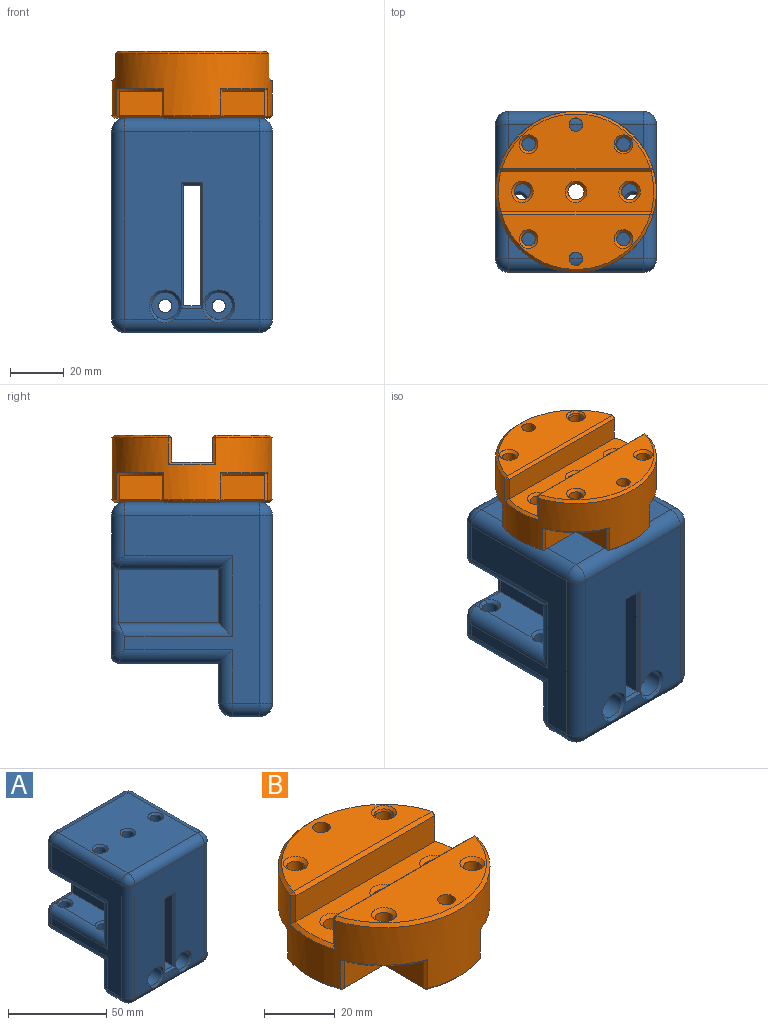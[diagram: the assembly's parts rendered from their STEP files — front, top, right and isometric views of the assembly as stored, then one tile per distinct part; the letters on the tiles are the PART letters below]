
ASSEMBLY  parts=2 mates=1
PART A: 144 faces, bbox 60x60x80 mm
  f0: plane 13.37x5mm, normal (0,-1,0), area 40mm2, adj f1,f139,f140,f141,f142,f143
  f1: cone r=5mm half-angle=45deg, axis (0,-1,0), area 39.8mm2, adj f0,f2,f137,f138
  f2: plane 70x50mm, normal (0,-1,0), area 2866.9mm2, adj f1,f3,f134,f135,f136,f139,f141,f142
  f3: plane 8x1mm, normal (0,-0.71,-0.71), area 9.9mm2, adj f2,f4,f139,f141
  f4: plane 56.5x15mm, normal (0,0,-1), area 627.2mm2, adj f3,f5,f8,f119,f120,f121,f130,f131
  f5: plane 46x1mm, normal (-0.71,0.71,0), area 64.3mm2, adj f4,f6,f121,f132
  f6: plane 8x1mm, normal (0,0.71,0.71), area 9.9mm2, adj f5,f7,f121,f130
  f7: plane 18x6mm, normal (0,0,1), area 108mm2, adj f6,f131,f132,f140
  f8: plane 37.5x30mm, normal (-1,0,0), area 1125mm2, adj f4,f9,f118,f121
  f9: cylinder r=5mm len=37.5mm, axis (0,-1,0), area 294.5mm2, adj f8,f10,f117,f121
  f10: plane 37.5x12.5mm, normal (0,0,-1), area 312.4mm2, adj f9,f11,f110,f111,f112,f113,f114,f115
  f11: cone r=3mm half-angle=45deg, axis (0,0,-1), area 19.1mm2, adj f10,f12,f15,f16
  f12: bspline ~3.87x1.5mm, area 5.3mm2, adj f11,f13,f16,f116
  f13: cone r=3mm half-angle=45deg, axis (0,0,-1), area 3.5mm2, adj f12,f14,f15,f16
  f14: plane 2.11x1.81mm, normal (0,0,-1), area 1.4mm2, adj f13,f110,f116
  f15: bspline ~2.78x1.35mm, area 3.8mm2, adj f11,f13,f16,f110
  f16: cylinder r=3mm len=13mm, axis (0,0,-1), area 245mm2, adj f11,f12,f13,f15,f17,f107,f108,f109
  f17: cone r=3mm half-angle=45deg, axis (0,0,1), area 19.1mm2, adj f16,f18,f107,f109
  f18: plane 37.5x12.5mm, normal (0,0,1), area 312.4mm2, adj f17,f19,f23,f97,f98,f99,f106,f113
  f19: cone r=4mm half-angle=45deg, axis (0,0,1), area 26.1mm2, adj f18,f20,f22
  f20: cylinder r=3mm len=13mm, axis (0,0,-1), area 245mm2, adj f19,f21,f22,f111
  f21: bspline ~3.87x1.5mm, area 5.3mm2, adj f20,f111,f112
  f22: bspline ~3.87x1.5mm, area 5.3mm2, adj f19,f20,f23
  f23: cylinder r=5mm len=19.25mm, axis (0,1,0), area 129.9mm2, adj f18,f22,f24,f96,f113
  f24: plane 70x50mm, normal (1,0,0), area 1396.3mm2, adj f23,f25,f90,f92,f94,f95,f96,f112
  f25: cylinder r=5mm len=20mm, axis (0,0,-1), area 137.4mm2, adj f24,f26,f112,f121
  f26: sphere r=5mm, area 39.3mm2, adj f25,f27,f90
  f27: cylinder r=5mm len=50mm, axis (-1,0,0), area 392.7mm2, adj f26,f28,f89,f121
  f28: sphere r=5mm, area 53.5mm2, adj f27,f29,f87
  f29: cylinder r=5mm len=20mm, axis (0,0,1), area 137.4mm2, adj f28,f30,f86,f121
  f30: cylinder r=5mm len=42.5mm, axis (0,-1,0), area 295.7mm2, adj f29,f31,f82,f83,f84,f85,f86
  f31: bspline ~5.97x5mm, area 13.6mm2, adj f30,f32,f81
  f32: cylinder r=5mm len=10mm, axis (0,0,-1), area 58.9mm2, adj f31,f33,f80,f86
  f33: bspline ~5.25x5mm, area 13.6mm2, adj f32,f34,f79
  f34: cylinder r=2.5mm len=15mm, axis (-1,0,0), area 53.2mm2, adj f33,f35,f65,f77,f78,f80
  f35: cylinder r=2.5mm len=32.5mm, axis (0,0,-1), area 211.1mm2, adj f34,f36,f38,f64,f80,f119,f120
  f36: torus R=2.5mm, axis (0,-1,0), area 25.2mm2, adj f35,f37,f80,f81
  f37: cylinder r=5mm len=37.5mm, axis (0,1,0), area 294.5mm2, adj f36,f83,f120,f121
  f38: cylinder r=2.5mm len=15mm, axis (1,0,0), area 54mm2, adj f35,f39,f62,f63
  f39: plane 37.5x12.5mm, normal (0,0,-1), area 418.5mm2, adj f38,f40,f42,f61,f64
  f40: plane 20x12.5mm, normal (0,1,0), area 250mm2, adj f39,f41,f64,f65
  f41: cylinder r=5mm len=30mm, axis (0,0,1), area 196.3mm2, adj f40,f42,f79,f86
  f42: cylinder r=5mm len=42.5mm, axis (0,-1,0), area 304.3mm2, adj f39,f41,f43,f63,f86
  f43: bspline ~3.65x3.65mm, area 1.9mm2, adj f42,f44
  f44: cylinder r=5mm len=17.5mm, axis (0,0,-1), area 127.6mm2, adj f43,f45,f62,f63,f86
  f45: sphere r=5mm, area 53.5mm2, adj f44,f46,f59
  f46: cylinder r=5mm len=50mm, axis (0,1,0), area 392.7mm2, adj f45,f47,f58,f86
  f47: plane 50x50mm, normal (0,0,1), area 2349.2mm2, adj f46,f48,f54,f56,f59,f92,f135
  f48: cone r=3mm half-angle=45deg, axis (0,0,1), area 31.1mm2, adj f47,f49
  f49: cylinder r=3mm len=23mm, axis (0,0,-1), area 433.5mm2, adj f48,f50
  f50: cone r=4mm half-angle=45deg, axis (0,0,-1), area 31.1mm2, adj f49,f51
  f51: plane 37.5x12.5mm, normal (0,0,-1), area 418.5mm2, adj f50,f52,f95,f97,f98
  f52: cylinder r=2.5mm len=15mm, axis (1,0,0), area 54mm2, adj f51,f53,f62,f118
  f53: bspline ~5.25x5mm, area 13.6mm2, adj f52,f94,f95
  f54: cone r=3mm half-angle=45deg, axis (0,0,1), area 31.1mm2, adj f47,f55
  f55: cylinder r=3mm len=23mm, axis (0,0,-1), area 433.5mm2, adj f54,f133
  f56: cone r=4mm half-angle=45deg, axis (0,0,1), area 31.1mm2, adj f47,f57
  f57: cylinder r=3mm len=23mm, axis (0,0,-1), area 433.5mm2, adj f56,f61
  f58: sphere r=5mm, area 39.3mm2, adj f46,f134,f135
  f59: cylinder r=5mm len=50mm, axis (-1,0,0), area 392.7mm2, adj f45,f47,f60,f62
  f60: sphere r=5mm, area 25mm2, adj f59,f92,f94
  f61: cone r=3mm half-angle=45deg, axis (0,0,-1), area 31.1mm2, adj f39,f57
  f62: plane 50x17.5mm, normal (0,1,0), area 875mm2, adj f38,f44,f52,f59,f94,f119
  f63: bspline ~4.67x3.48mm, area 8.4mm2, adj f38,f42,f44
  f64: plane 37.5x20mm, normal (-1,0,0), area 750mm2, adj f35,f39,f40,f65
  f65: plane 37.5x12.5mm, normal (0,0,1), area 369.9mm2, adj f34,f40,f64,f66,f73,f79
  f66: cone r=3mm half-angle=45deg, axis (0,0,1), area 19.1mm2, adj f65,f67,f69,f77
  f67: bspline ~3.87x1.5mm, area 5.3mm2, adj f66,f68,f69,f79
  f68: cone r=3mm half-angle=45deg, axis (0,0,1), area 3.5mm2, adj f67,f69,f77,f78
  f69: cylinder r=3mm len=13mm, axis (0,0,-1), area 245mm2, adj f66,f67,f68,f70,f71,f72,f77,f84
  f70: bspline ~2.78x1.35mm, area 3.8mm2, adj f69,f71,f72,f81
  f71: cone r=4mm half-angle=45deg, axis (0,0,-1), area 19.1mm2, adj f69,f70,f83,f84
  f72: cone r=4mm half-angle=45deg, axis (0,0,-1), area 3.5mm2, adj f69,f70,f84,f85
  f73: cone r=4mm half-angle=45deg, axis (0,0,1), area 26.1mm2, adj f65,f74,f76
  f74: cylinder r=3mm len=13mm, axis (0,0,-1), area 245mm2, adj f73,f75,f76,f82
  f75: cone r=3mm half-angle=45deg, axis (0,0,-1), area 26.1mm2, adj f74,f82,f83
  f76: bspline ~3.87x1.5mm, area 5.3mm2, adj f73,f74,f79
  f77: bspline ~2.78x1.35mm, area 3.8mm2, adj f34,f66,f68,f69
  f78: plane 2.11x1.81mm, normal (0,0,1), area 1.4mm2, adj f34,f68,f79
  f79: cylinder r=5mm len=42.5mm, axis (0,1,0), area 295.7mm2, adj f33,f41,f65,f67,f76,f78,f86
  f80: plane 15x10mm, normal (0,1,0), area 148.7mm2, adj f32,f34,f35,f36,f81
  f81: cylinder r=2.5mm len=12.5mm, axis (1,0,0), area 48.3mm2, adj f31,f36,f70,f80,f83,f85
  f82: bspline ~3.87x1.5mm, area 5.3mm2, adj f30,f74,f75
  f83: plane 37.5x12.5mm, normal (0,0,-1), area 369.9mm2, adj f30,f37,f71,f75,f81,f121
  f84: bspline ~3.87x1.5mm, area 5.3mm2, adj f30,f69,f71,f72
  f85: plane 2.11x1.81mm, normal (0,0,-1), area 1.4mm2, adj f30,f72,f81
  f86: plane 70x50mm, normal (-1,0,0), area 1500mm2, adj f29,f30,f32,f41,f42,f44,f46,f79
  f87: cylinder r=5mm len=10mm, axis (0,-1,0), area 78.5mm2, adj f28,f86,f88,f89
  f88: sphere r=5mm, area 39.3mm2, adj f87,f134,f143
  f89: plane 50x10mm, normal (0,0,-1), area 500mm2, adj f27,f87,f90,f143
  f90: cylinder r=5mm len=10mm, axis (0,1,0), area 78.5mm2, adj f24,f26,f89,f91
  f91: sphere r=5mm, area 39.3mm2, adj f90,f136,f143
  f92: cylinder r=5mm len=50mm, axis (0,-1,0), area 392.7mm2, adj f24,f47,f60,f93
  f93: sphere r=5mm, area 39.3mm2, adj f92,f135,f136
  f94: cylinder r=5mm len=17.5mm, axis (0,0,1), area 127.6mm2, adj f24,f53,f60,f62
  f95: cylinder r=5mm len=42.5mm, axis (0,-1,0), area 304.3mm2, adj f24,f51,f53,f96
  f96: cylinder r=5mm len=30mm, axis (0,0,-1), area 196.3mm2, adj f23,f24,f95,f97
  f97: plane 20x12.5mm, normal (0,1,0), area 250mm2, adj f18,f51,f96,f98
  f98: plane 37.5x20mm, normal (1,0,0), area 750mm2, adj f18,f51,f97,f118
  f99: cylinder r=2.5mm len=15mm, axis (-1,0,0), area 53.2mm2, adj f18,f100,f104,f105,f109,f118
  f100: plane 15x10mm, normal (0,1,0), area 148.7mm2, adj f99,f101,f110,f117,f118
  f101: cylinder r=5mm len=10mm, axis (0,0,1), area 58.9mm2, adj f100,f102,f103,f104
  f102: bspline ~5.97x5mm, area 13.6mm2, adj f101,f110,f116
  f103: plane 9.25x5mm, normal (1,0,0), area 46.2mm2, adj f101,f106,f115,f116
  f104: bspline ~5.97x5mm, area 13.6mm2, adj f99,f101,f106
  f105: plane 2.11x1.81mm, normal (0,0,1), area 1.4mm2, adj f99,f106,f108
  f106: cylinder r=5mm len=11.75mm, axis (0,1,0), area 80.8mm2, adj f18,f103,f104,f105,f107,f115
  f107: bspline ~3.87x1.5mm, area 5.3mm2, adj f16,f17,f106,f108
  f108: cone r=3mm half-angle=45deg, axis (0,0,1), area 3.5mm2, adj f16,f105,f107,f109
  f109: bspline ~2.78x1.35mm, area 3.8mm2, adj f16,f17,f99,f108
  f110: cylinder r=2.5mm len=12.5mm, axis (1,0,0), area 48.3mm2, adj f10,f14,f15,f100,f102,f117
  f111: cone r=4mm half-angle=45deg, axis (0,0,-1), area 26.1mm2, adj f10,f20,f21
  f112: cylinder r=5mm len=19.25mm, axis (0,1,0), area 129.9mm2, adj f10,f21,f24,f25,f113
  f113: plane 15x10mm, normal (0,1,0), area 139.3mm2, adj f10,f18,f23,f24,f112,f114
  f114: plane 15x11.5mm, normal (1,0,0), area 172.5mm2, adj f10,f18,f113,f115
  f115: plane 15x10mm, normal (0,-1,0), area 139.3mm2, adj f10,f18,f103,f106,f114,f116
  f116: cylinder r=5mm len=11.75mm, axis (0,1,0), area 80.8mm2, adj f10,f12,f14,f102,f103,f115
  f117: torus R=2.5mm, axis (0,-1,0), area 25.2mm2, adj f9,f100,f110,f118
  f118: cylinder r=2.5mm len=32.5mm, axis (0,0,1), area 211.1mm2, adj f8,f52,f98,f99,f100,f117,f119
  f119: cylinder r=2.5mm len=20mm, axis (1,0,0), area 68.7mm2, adj f4,f35,f62,f118
  f120: plane 37.5x30mm, normal (1,0,0), area 1125mm2, adj f4,f35,f37,f121
  f121: plane 50x50mm, normal (0,1,0), area 840.8mm2, adj f4,f5,f6,f8,f9,f10,f25,f27
  f122: cone r=2.5mm half-angle=45deg, axis (0,1,0), area 26.7mm2, adj f121,f123
  f123: cylinder r=2.5mm len=11.5mm, axis (0,1,0), area 180.6mm2, adj f122,f124
  f124: plane 10x10mm, normal (0,-1,0), area 58.9mm2, adj f123,f125
  f125: cylinder r=5mm len=10mm, axis (0,-1,0), area 203.8mm2, adj f124,f126,f142
  f126: bspline ~6.63x2.08mm, area 10mm2, adj f125,f142,f143
  f127: cone r=3.5mm half-angle=45deg, axis (0,1,0), area 26.7mm2, adj f121,f128
  f128: cylinder r=2.5mm len=11.5mm, axis (0,1,0), area 180.6mm2, adj f127,f129
  f129: plane 10x10mm, normal (0,-1,0), area 58.9mm2, adj f128,f137
  f130: plane 46x1mm, normal (0.71,0.71,0), area 64.3mm2, adj f4,f6,f121,f131
  f131: plane 45x18mm, normal (1,0,0), area 810mm2, adj f4,f7,f130,f139
  f132: plane 45x18mm, normal (-1,0,0), area 810mm2, adj f4,f5,f7,f141
  f133: cone r=4mm half-angle=45deg, axis (0,0,-1), area 31.1mm2, adj f4,f55
  f134: cylinder r=5mm len=70mm, axis (0,0,1), area 549.8mm2, adj f2,f58,f86,f88
  f135: cylinder r=5mm len=50mm, axis (1,0,0), area 392.7mm2, adj f2,f47,f58,f93
  f136: cylinder r=5mm len=70mm, axis (0,0,-1), area 549.8mm2, adj f2,f24,f91,f93
  f137: cylinder r=5mm len=10mm, axis (0,-1,0), area 203.8mm2, adj f1,f129,f138
  f138: bspline ~6.63x2.08mm, area 10mm2, adj f1,f137,f143
  f139: plane 47x1mm, normal (0.71,-0.71,0), area 65.1mm2, adj f0,f2,f3,f131,f140
  f140: plane 8x1mm, normal (0,-0.71,0.71), area 9.9mm2, adj f0,f7,f139,f141
  f141: plane 47x1mm, normal (-0.71,-0.71,0), area 65.1mm2, adj f0,f2,f3,f132,f140
  f142: cone r=5mm half-angle=45deg, axis (0,-1,0), area 39.8mm2, adj f0,f2,f125,f126
  f143: cylinder r=5mm len=50mm, axis (-1,0,0), area 381.4mm2, adj f0,f2,f88,f89,f91,f126,f138
PART B: 83 faces, bbox 60x60x25 mm
  f0: plane 58x58mm, normal (0,0,-1), area 1669.7mm2, adj f35,f36,f37,f52,f53,f54,f55,f58
  f1: plane 58x15.57mm, normal (0,0,1), area 709.6mm2, adj f23,f24,f30,f31,f32,f42,f43,f44
  f2: plane 55.45x20.5mm, normal (0,0,1), area 738.6mm2, adj f10,f33,f34,f38,f39
  f3: cylinder r=30mm len=60mm, axis (0,0,-1), area 2954.1mm2, adj f39,f42,f43,f44,f45,f46,f47,f48
  f4: cylinder r=2.5mm len=13mm, axis (0,0,1), area 204.2mm2, adj f28,f60
  f5: cylinder r=2.5mm len=12.59mm, axis (0,0,1), area 197.7mm2, adj f56,f57
  f6: cylinder r=2.5mm len=13mm, axis (0,0,1), area 204.2mm2, adj f33,f61
  f7: cylinder r=2.5mm len=13mm, axis (0,0,1), area 204.2mm2, adj f34,f62
  f8: plane 55.45x20.5mm, normal (0,0,1), area 738.6mm2, adj f9,f28,f29,f48,f51
  f9: cylinder r=2.5mm len=24mm, axis (0,0,-1), area 377mm2, adj f8,f58
  f10: cylinder r=2.5mm len=24mm, axis (0,0,-1), area 377mm2, adj f2,f59
  f11: plane 15.98x9.37mm, normal (0,-1,0), area 143.9mm2, adj f12,f13,f79,f81,f82
  f12: plane 15.98x9.37mm, normal (-1,0,0), area 143.9mm2, adj f11,f13,f78,f79,f80
  f13: plane 15.58x15.58mm, normal (0,0,-1), area 115.1mm2, adj f11,f12,f62,f79
  f14: plane 15.98x9.37mm, normal (1,0,0), area 143.9mm2, adj f15,f16,f65,f66,f67
  f15: plane 15.98x9.37mm, normal (0,-1,0), area 143.9mm2, adj f14,f16,f63,f64,f65
  f16: plane 15.58x15.58mm, normal (0,0,-1), area 115.1mm2, adj f14,f15,f61,f65
  f17: plane 15.98x9.37mm, normal (0,1,0), area 143.9mm2, adj f18,f19,f68,f69,f70
  f18: plane 15.98x9.37mm, normal (1,0,0), area 143.9mm2, adj f17,f19,f69,f71,f72
  f19: plane 15.58x15.58mm, normal (0,0,-1), area 115.1mm2, adj f17,f18,f57,f69
  f20: plane 15.98x9.37mm, normal (-1,0,0), area 143.9mm2, adj f21,f22,f74,f76,f77
  f21: plane 15.98x9.37mm, normal (0,1,0), area 143.9mm2, adj f20,f22,f73,f75,f77
  f22: plane 15.58x15.58mm, normal (0,0,-1), area 115.1mm2, adj f20,f21,f60,f77
  f23: plane 55.45x9mm, normal (0,-1,0), area 499.1mm2, adj f1,f46,f47,f51
  f24: plane 55.45x9mm, normal (0,1,0), area 499.1mm2, adj f1,f38,f42,f43
  f25: cylinder r=3mm len=13mm, axis (0,0,1), area 245mm2, adj f30,f37
  f26: cylinder r=3mm len=13mm, axis (0,0,1), area 245mm2, adj f31,f36
  f27: cylinder r=3mm len=13mm, axis (0,0,1), area 245mm2, adj f32,f35
  f28: cone r=2.5mm half-angle=45deg, axis (0,0,1), area 26.7mm2, adj f4,f8
  f29: cone r=3.5mm half-angle=45deg, axis (0,0,1), area 19.8mm2, adj f8,f56
  f30: cone r=3mm half-angle=45deg, axis (0,0,1), area 31.1mm2, adj f1,f25
  f31: cone r=3mm half-angle=45deg, axis (0,0,1), area 31.1mm2, adj f1,f26
  f32: cone r=4mm half-angle=45deg, axis (0,0,1), area 31.1mm2, adj f1,f27
  f33: cone r=2.5mm half-angle=45deg, axis (0,0,1), area 26.7mm2, adj f2,f6
  f34: cone r=3.5mm half-angle=45deg, axis (0,0,1), area 26.7mm2, adj f2,f7
  f35: cone r=3mm half-angle=45deg, axis (0,0,-1), area 31.1mm2, adj f0,f27
  f36: cone r=4mm half-angle=45deg, axis (0,0,-1), area 31.1mm2, adj f0,f26
  f37: cone r=4mm half-angle=45deg, axis (0,0,-1), area 31.1mm2, adj f0,f25
  f38: plane 55.45x1mm, normal (0,0.71,0.71), area 78.4mm2, adj f2,f24,f40,f41
  f39: cone r=29mm half-angle=45deg, axis (0,0,-1), area 106.2mm2, adj f2,f3,f40,f41
  f40: plane 1.29x1mm, normal (0.69,0.51,0.51), area 0.9mm2, adj f38,f39,f42
  f41: plane 1.29x1mm, normal (-0.69,0.51,0.51), area 0.9mm2, adj f38,f39,f43
  f42: plane 10.01x1.31mm, normal (0.8,0.59,0), area 15.1mm2, adj f1,f3,f24,f40,f44
  f43: plane 10.01x1.31mm, normal (-0.8,0.59,0), area 15.1mm2, adj f1,f3,f24,f41,f45
  f44: cone r=29mm half-angle=45deg, axis (0,0,-1), area 23.8mm2, adj f1,f3,f42,f46
  f45: cone r=29mm half-angle=45deg, axis (0,0,-1), area 23.8mm2, adj f1,f3,f43,f47
  f46: plane 10.01x1.31mm, normal (0.8,-0.59,0), area 15.1mm2, adj f1,f3,f23,f44,f49
  f47: plane 10.01x1.31mm, normal (-0.8,-0.59,0), area 15.1mm2, adj f1,f3,f23,f45,f50
  f48: cone r=29mm half-angle=45deg, axis (0,0,-1), area 106.2mm2, adj f3,f8,f49,f50
  f49: plane 1.29x1mm, normal (0.69,-0.51,0.51), area 0.9mm2, adj f46,f48,f51
  f50: plane 1.29x1mm, normal (-0.69,-0.51,0.51), area 0.9mm2, adj f47,f48,f51
  f51: plane 55.45x1mm, normal (0,-0.71,0.71), area 78.4mm2, adj f8,f23,f49,f50
  f52: cone r=30mm half-angle=45deg, axis (0,0,1), area 30.6mm2, adj f0,f3,f71,f72,f74,f76
  f53: cone r=30mm half-angle=45deg, axis (0,0,1), area 30.6mm2, adj f0,f3,f63,f64,f68,f70
  f54: cone r=30mm half-angle=45deg, axis (0,0,1), area 30.6mm2, adj f0,f3,f66,f67,f78,f80
  f55: cone r=30mm half-angle=45deg, axis (0,0,1), area 30.6mm2, adj f0,f3,f73,f75,f81,f82
  f56: cone r=2.5mm half-angle=22.5deg, axis (0,0,1), area 12.7mm2, adj f5,f29
  f57: cone r=3.5mm half-angle=45deg, axis (0,0,-1), area 26.7mm2, adj f5,f19
  f58: cone r=3.5mm half-angle=45deg, axis (0,0,-1), area 26.7mm2, adj f0,f9
  f59: cone r=2.5mm half-angle=45deg, axis (0,0,-1), area 26.7mm2, adj f0,f10
  f60: cone r=3.5mm half-angle=45deg, axis (0,0,-1), area 26.7mm2, adj f4,f22
  f61: cone r=2.5mm half-angle=45deg, axis (0,0,-1), area 26.7mm2, adj f6,f16
  f62: cone r=3.5mm half-angle=45deg, axis (0,0,-1), area 26.7mm2, adj f7,f13
  f63: plane 10.34x0.95mm, normal (0.57,-0.82,0), area 11.2mm2, adj f3,f15,f53,f64,f65
  f64: plane 17.45x1mm, normal (0,-0.71,-0.71), area 23.6mm2, adj f0,f15,f53,f63,f66
  f65: cone r=29mm half-angle=45deg, axis (0,0,1), area 33.7mm2, adj f3,f14,f15,f16,f63,f67
  f66: plane 17.45x1mm, normal (0.71,0,-0.71), area 23.6mm2, adj f0,f14,f54,f64,f67
  f67: plane 10.34x0.95mm, normal (0.82,-0.57,0), area 11.2mm2, adj f3,f14,f54,f65,f66
  f68: plane 10.34x0.95mm, normal (0.57,0.82,0), area 11.2mm2, adj f3,f17,f53,f69,f70
  f69: cone r=29mm half-angle=45deg, axis (0,0,1), area 33.7mm2, adj f3,f17,f18,f19,f68,f71
  f70: plane 17.45x1mm, normal (0,0.71,-0.71), area 23.6mm2, adj f0,f17,f53,f68,f72
  f71: plane 10.34x0.95mm, normal (0.82,0.57,0), area 11.2mm2, adj f3,f18,f52,f69,f72
  f72: plane 17.45x1mm, normal (0.71,0,-0.71), area 23.6mm2, adj f0,f18,f52,f70,f71
  f73: plane 17.45x1mm, normal (0,0.71,-0.71), area 23.6mm2, adj f0,f21,f55,f74,f75
  f74: plane 17.45x1mm, normal (-0.71,0,-0.71), area 23.6mm2, adj f0,f20,f52,f73,f76
  f75: plane 10.34x0.95mm, normal (-0.57,0.82,0), area 11.2mm2, adj f3,f21,f55,f73,f77
  f76: plane 10.34x0.95mm, normal (-0.82,0.57,0), area 11.2mm2, adj f3,f20,f52,f74,f77
  f77: cone r=29mm half-angle=45deg, axis (0,0,1), area 33.7mm2, adj f3,f20,f21,f22,f75,f76
  f78: plane 10.34x0.95mm, normal (-0.82,-0.57,0), area 11.2mm2, adj f3,f12,f54,f79,f80
  f79: cone r=29mm half-angle=45deg, axis (0,0,1), area 33.7mm2, adj f3,f11,f12,f13,f78,f81
  f80: plane 17.45x1mm, normal (-0.71,0,-0.71), area 23.6mm2, adj f0,f12,f54,f78,f82
  f81: plane 10.34x0.95mm, normal (-0.57,-0.82,0), area 11.2mm2, adj f3,f11,f55,f79,f82
  f82: plane 17.45x1mm, normal (0,-0.71,-0.71), area 23.6mm2, adj f0,f11,f55,f80,f81
PLACE A t=(-82.64,-10.84,-33.03)mm
PLACE B t=(-82.64,-10.84,6.97)mm fixed
MATE fastened A.f54 <-> B.f3  axis (0,0,1) through (-82.64,-10.84,6.97)mm
